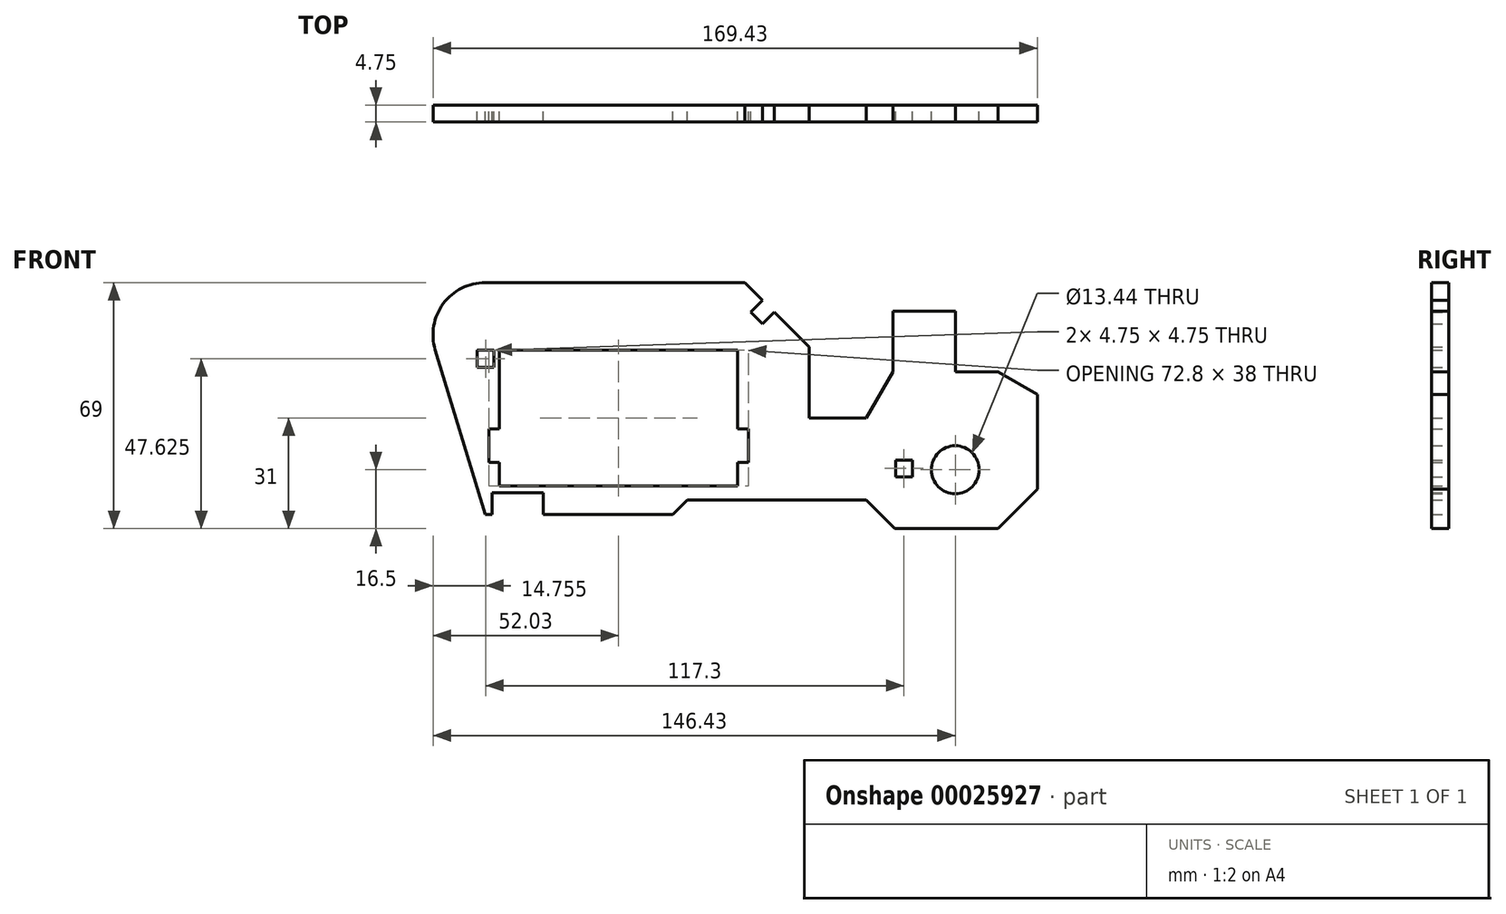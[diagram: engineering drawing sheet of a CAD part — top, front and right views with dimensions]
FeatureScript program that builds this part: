
annotation { "Feature Type Name" : "Feature", "Feature Type Description" : "" }
export const myFeature = defineFeature(function(context is Context, id is Id, definition is map)
    precondition{}
    {
        {
            var Q0;
            Q0=qCreatedBy(makeId("Front.planeOp"),FACE);
            var sketch = newSketch(context, id + "F0", { "sketchPlane" : qUnion([Q0])});
            skLineSegment(sketch, "E0.bottom", {"start": v(0, 0) * mm, "end": v(66.8, 0) * mm});
            skLineSegment(sketch, "E0.top", {"start": v(0, 38) * mm, "end": v(66.8, 38) * mm});
            skLineSegment(sketch, "E0.left", {"start": v(0, 0) * mm, "end": v(0, 6.5) * mm});
            skLineSegment(sketch, "E0.right", {"start": v(66.8, 0) * mm, "end": v(66.8, 6.5) * mm});
            skLineSegment(sketch, "E1", {"start": v(-4, -8) * mm, "end": v(-2, -8) * mm});
            skLineSegment(sketch, "E2", {"start": v(48.64, -8) * mm, "end": v(52.64, -4) * mm});
            skLineSegment(sketch, "E3", {"start": v(52.64, -4) * mm, "end": v(102.8, -4) * mm});
            skLineSegment(sketch, "E4", {"start": v(102.8, -4) * mm, "end": v(110.8, -12) * mm});
            skLineSegment(sketch, "E5", {"start": v(110.8, -12) * mm, "end": v(139.8, -12) * mm});
            skLineSegment(sketch, "E6", {"start": v(139.8, -12) * mm, "end": v(150.8, -1) * mm});
            skLineSegment(sketch, "E7", {"start": v(150.8, 3) * mm, "end": v(150.8, 8) * mm});
            skLineSegment(sketch, "E8", {"start": v(150.8, 25.65) * mm, "end": v(139.8, 32) * mm});
            skLineSegment(sketch, "E9", {"start": v(139.8, 32) * mm, "end": v(127.8, 32) * mm});
            skLineSegment(sketch, "E10", {"start": v(127.8, 32) * mm, "end": v(127.8, 49) * mm});
            skLineSegment(sketch, "E11", {"start": v(127.8, 49) * mm, "end": v(110.3, 49) * mm});
            skLineSegment(sketch, "E12", {"start": v(110.3, 49) * mm, "end": v(110.3, 32) * mm});
            skLineSegment(sketch, "E13", {"start": v(110.3, 32) * mm, "end": v(102.8, 19) * mm});
            skLineSegment(sketch, "E14", {"start": v(102.8, 19) * mm, "end": v(86.8, 19) * mm});
            skLineSegment(sketch, "E15", {"start": v(86.8, 19) * mm, "end": v(86.8, 39) * mm});
            skLineSegment(sketch, "E16", {"start": v(86.8, 39) * mm, "end": v(77.07, 48.73) * mm});
            skLineSegment(sketch, "E17", {"start": v(68.8, 57) * mm, "end": v(-4, 57) * mm});
            skArc(sketch, "E18", {"start": v(-4, 57) * mm, "mid": v(-15.75, 51.08) * mm, "end": v(-18, 38.12) * mm});
            skLineSegment(sketch, "E19", {"start": v(-18, 38.12) * mm, "end": v(-4, -8) * mm});
            skCircle(sketch, "E20", {"center": v(127.8, 4.5) * mm, "radius": 6.72 * mm});
            skLineSegment(sketch, "E21.trimOffspring", {"start": v(150.8, 11.99) * mm, "end": v(150.8, 25.65) * mm});
            skLineSegment(sketch, "E22", {"start": v(77.07, 48.73) * mm, "end": v(73.71, 45.37) * mm});
            skLineSegment(sketch, "E23", {"start": v(73.71, 45.37) * mm, "end": v(70.4, 48.7) * mm});
            skLineSegment(sketch, "E24", {"start": v(70.4, 48.7) * mm, "end": v(73.75, 52.05) * mm});
            skLineSegment(sketch, "E25.trimOffspring", {"start": v(73.75, 52.05) * mm, "end": v(68.8, 57) * mm});
            skLineSegment(sketch, "E26", {"start": v(66.8, 6.5) * mm, "end": v(69.8, 6.5) * mm});
            skLineSegment(sketch, "E27", {"start": v(69.8, 6.5) * mm, "end": v(69.8, 16) * mm});
            skLineSegment(sketch, "E28", {"start": v(69.8, 16) * mm, "end": v(66.8, 16) * mm});
            skLineSegment(sketch, "E29", {"start": v(0, 6.5) * mm, "end": v(-3, 6.5) * mm});
            skLineSegment(sketch, "E30", {"start": v(-3, 6.5) * mm, "end": v(-3, 16) * mm});
            skLineSegment(sketch, "E31", {"start": v(-3, 16) * mm, "end": v(0, 16) * mm});
            skLineSegment(sketch, "E32.trimOffspring", {"start": v(0, 16) * mm, "end": v(0, 38) * mm});
            skLineSegment(sketch, "E33.trimOffspring", {"start": v(66.8, 16) * mm, "end": v(66.8, 38) * mm});
            skLineSegment(sketch, "E34.bottom", {"start": v(-1.5, 38) * mm, "end": v(-6.25, 38) * mm});
            skLineSegment(sketch, "E34.top", {"start": v(-1.5, 33.25) * mm, "end": v(-6.25, 33.25) * mm});
            skLineSegment(sketch, "E34.left", {"start": v(-1.5, 38) * mm, "end": v(-1.5, 33.25) * mm});
            skLineSegment(sketch, "E34.right", {"start": v(-6.25, 38) * mm, "end": v(-6.25, 33.25) * mm});
            skLineSegment(sketch, "E35.bottom", {"start": v(111.05, 7.25) * mm, "end": v(115.8, 7.25) * mm});
            skLineSegment(sketch, "E35.top", {"start": v(111.05, 2.5) * mm, "end": v(115.8, 2.5) * mm});
            skLineSegment(sketch, "E35.left", {"start": v(111.05, 7.25) * mm, "end": v(111.05, 2.5) * mm});
            skLineSegment(sketch, "E35.right", {"start": v(115.8, 7.25) * mm, "end": v(115.8, 2.5) * mm});
            skLineSegment(sketch, "E36", {"start": v(-2, -8) * mm, "end": v(-2, -2) * mm});
            skLineSegment(sketch, "E37", {"start": v(-2, -2) * mm, "end": v(12.25, -2) * mm});
            skLineSegment(sketch, "E38", {"start": v(12.25, -2) * mm, "end": v(12.25, -8) * mm});
            skLineSegment(sketch, "E39.trimOffspring", {"start": v(12.25, -8) * mm, "end": v(48.64, -8) * mm});
            skLineSegment(sketch, "E40", {"start": v(150.8, 11.99) * mm, "end": v(150.8, 8) * mm});
            skLineSegment(sketch, "E41", {"start": v(150.8, 3) * mm, "end": v(150.8, -1) * mm});
            skSolve(sketch);
        }
        {
            var Q0;
            Q0 = qSketchRegion(id + "F0", true);
            extrude(context, id + "F1", {"entities" : qUnion([Q0]), "depth" : 4.75 * mm});
        }
    });
